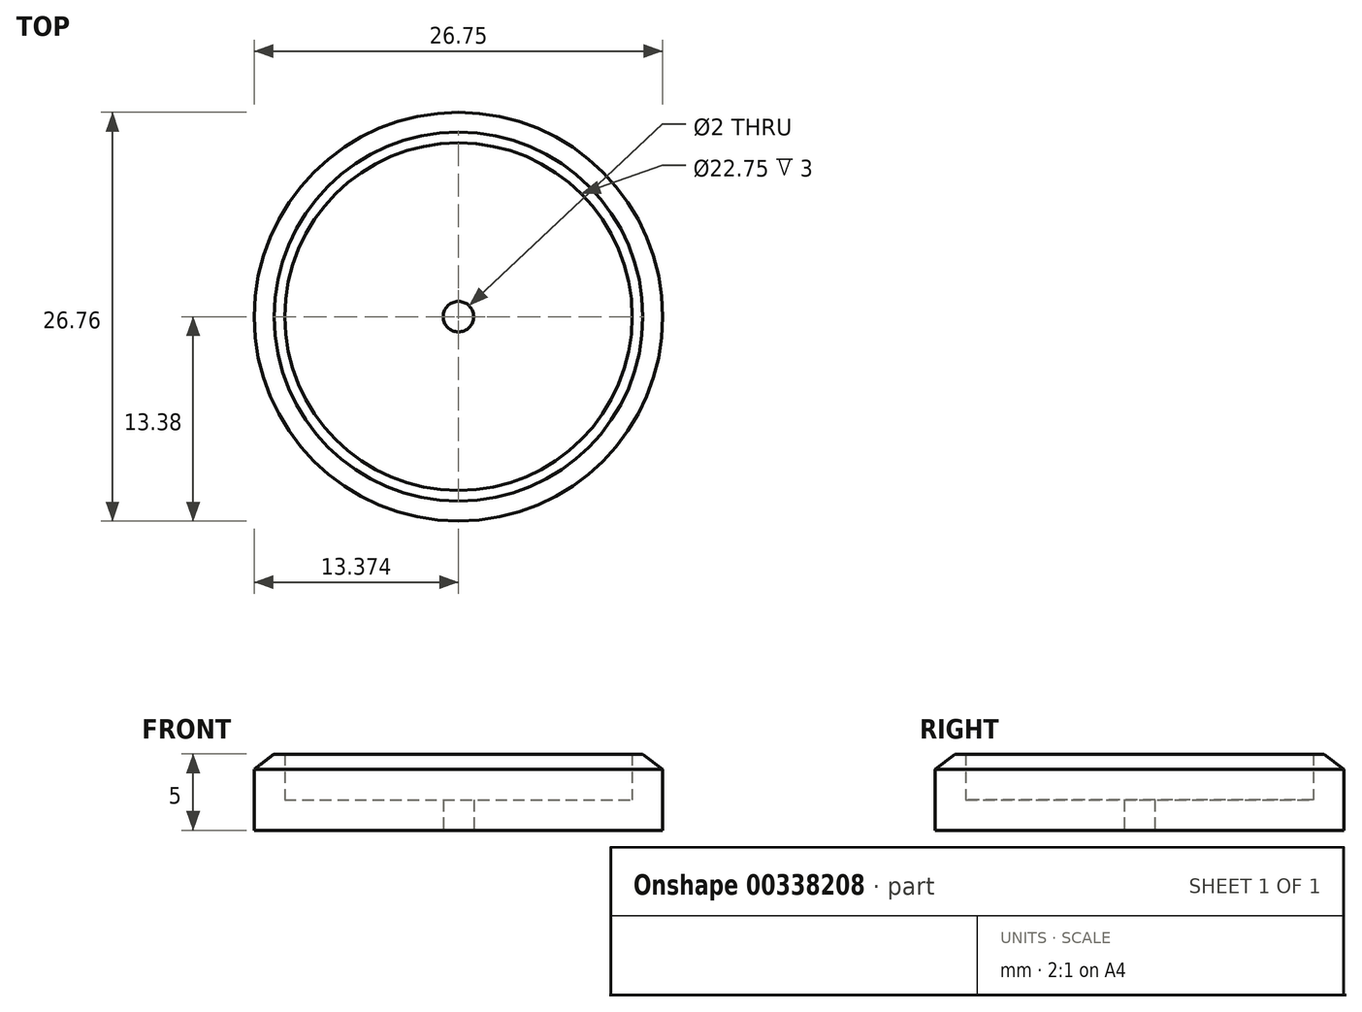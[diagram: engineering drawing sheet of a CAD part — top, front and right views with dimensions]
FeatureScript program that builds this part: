
annotation { "Feature Type Name" : "Feature", "Feature Type Description" : "" }
export const myFeature = defineFeature(function(context is Context, id is Id, definition is map)
    precondition{}
    {
        {
            var Q0;
            Q0=qCreatedBy(makeId("Front.planeOp"),FACE);
            var sketch = newSketch(context, id + "F0", { "sketchPlane" : qUnion([Q0])});
            skLineSegment(sketch, "E0", {"start": v(6.25, -3.94) * mm, "end": v(6.25, -1.94) * mm, "construction": true});
            skLineSegment(sketch, "E1", {"start": v(6.25, -3.94) * mm, "end": v(5.25, -3.94) * mm, "construction": true});
            skLineSegment(sketch, "E2", {"start": v(5.25, -3.94) * mm, "end": v(5.25, -1.94) * mm, "construction": true});
            skLineSegment(sketch, "E3", {"start": v(5.25, -1.94) * mm, "end": v(6.25, -1.94) * mm, "construction": true});
            skLineSegment(sketch, "E4", {"start": v(5.25, -3.94) * mm, "end": v(-7.12, -3.94) * mm});
            skLineSegment(sketch, "E5", {"start": v(5.25, -1.94) * mm, "end": v(-5.12, -1.94) * mm});
            skLineSegment(sketch, "E6", {"start": v(-7.12, 0.06) * mm, "end": v(-7.12, -3.94) * mm});
            skLineSegment(sketch, "E7", {"start": v(-7.12, 0.06) * mm, "end": v(-5.82, 1.06) * mm});
            skLineSegment(sketch, "E8", {"start": v(-5.82, 1.06) * mm, "end": v(-5.12, 1.06) * mm});
            skLineSegment(sketch, "E9", {"start": v(5.25, -1.94) * mm, "end": v(5.25, -3.94) * mm});
            skPoint(sketch, "E10.end.orphan", {"position": v(-5.12, 0.06) * mm});
            skLineSegment(sketch, "E11", {"start": v(-5.12, -1.94) * mm, "end": v(-5.12, 1.06) * mm});
            skSolve(sketch);
        }
        {
            var Q0;
            Q0 = qSketchRegion(id + "F0", true);
            var Q1;
            Q1=sQuery(id+"F0.wireOp",EDGE,"E0");
            revolve(context, id + "F1", {"entities" : qUnion([Q0]), "axis" : qUnion([Q1]), "revolveType" : RevolveType.FULL});
        }
    });
